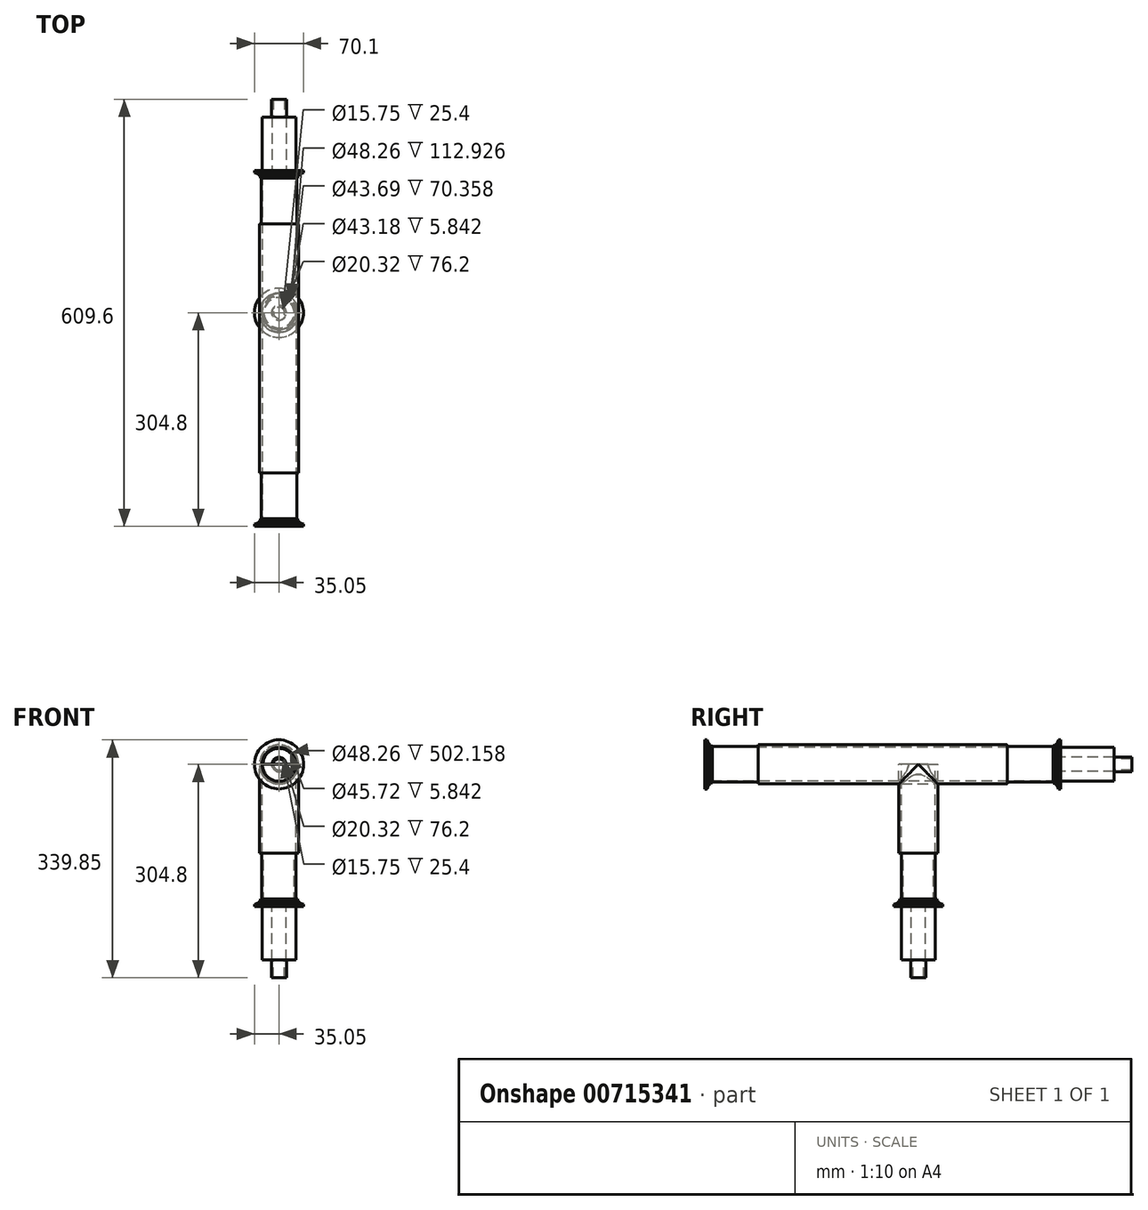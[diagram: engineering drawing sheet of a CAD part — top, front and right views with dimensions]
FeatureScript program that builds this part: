
annotation { "Feature Type Name" : "Feature", "Feature Type Description" : "" }
export const myFeature = defineFeature(function(context is Context, id is Id, definition is map)
    precondition{}
    {
        {
            var Q0;
            Q0=qCreatedBy(makeId("Front.planeOp"),FACE);
            var sketch = newSketch(context, id + "F0", { "sketchPlane" : qUnion([Q0])});
            skCircle(sketch, "E0", {"center": v(0, 0) * mm, "radius": 22.23 * mm, "construction": true});
            skSolve(sketch);
        }
        {
            var Q0;
            Q0=qCreatedBy(makeId("Front.planeOp"),FACE);
            var sketch = newSketch(context, id + "F1", { "sketchPlane" : qUnion([Q0])});
            skCircle(sketch, "E1", {"center": v(0, 0) * mm, "radius": 24.13 * mm});
            skCircle(sketch, "E2", {"center": v(0, 0) * mm, "radius": 35.05 * mm});
            skSolve(sketch);
        }
        {
            var Q0;
            Q0=qSketchRegion(id+"F1",true);
            extrude(context, id + "F2", {"entities" : qUnion([Q0]), "oppositeDirection" : true, "depth" : 5.84 * mm, "offsetDistance" : 25.4 * mm});
        }
        {
            var Q0;
            Q0=makeQuery(id+"F2.opExtrude","CAP_EDGE",EDGE,{"disambiguationData":[OSD([sQuery(id+"F1.wireOp",EDGE,"E2")])],"isStart":false});
            chamfer(context, id + "F3", {"entities" : qUnion([Q0]), "chamferType" : ChamferType.OFFSET_ANGLE, "width" : 2.54 * mm, "oppositeDirection" : false, "angle" : 70 * degree, "tangentPropagation" : true});
        }
        {
            var Q0;
            Q0=makeQuery(id+"F2.opExtrude","CAP_FACE",FACE,{"disambiguationData":[OSD([sQuery(id+"F1.wireOp",EDGE,"E1"),sQuery(id+"F1.wireOp",EDGE,"E2")])],"isStart":false});
            var sketch = newSketch(context, id + "F4", { "sketchPlane" : qUnion([Q0])});
            skCircle(sketch, "E3", {"center": v(0, 0) * mm, "radius": 28.07 * mm});
            skCircle(sketch, "E4", {"center": v(0, 0) * mm, "radius": 24.13 * mm});
            skSolve(sketch);
        }
        {
            var Q0;
            Q0=qSketchRegion(id+"F4",true);
            extrude(context, id + "F5", {"entities" : qUnion([Q0]), "operationType" : NewBodyOperationType.ADD, "depth" : 2.54 * mm, "offsetDistance" : 25.4 * mm});
        }
        {
            var Q0;
            Q0=makeQuery(id+"F5.opExtrude","CAP_FACE",FACE,{"disambiguationData":[OSD([sQuery(id+"F4.wireOp",EDGE,"E3"),sQuery(id+"F4.wireOp",EDGE,"E4")])],"isStart":false});
            var sketch = newSketch(context, id + "F6", { "sketchPlane" : qUnion([Q0])});
            skCircle(sketch, "E5", {"center": v(0, 0) * mm, "radius": 26.55 * mm});
            skCircle(sketch, "E6", {"center": v(0, 0) * mm, "radius": 24.13 * mm});
            skSolve(sketch);
        }
        {
            var Q0;
            Q0=qSketchRegion(id+"F6",true);
            extrude(context, id + "F7", {"entities" : qUnion([Q0]), "operationType" : NewBodyOperationType.ADD, "depth" : 2.54 * mm, "offsetDistance" : 25.4 * mm});
        }
        {
            var Q0;
            Q0=makeQuery(id+"F7.opExtrude","CAP_FACE",FACE,{"disambiguationData":[OSD([sQuery(id+"F6.wireOp",EDGE,"E5"),sQuery(id+"F6.wireOp",EDGE,"E6")])],"isStart":false});
            var sketch = newSketch(context, id + "F8", { "sketchPlane" : qUnion([Q0])});
            skCircle(sketch, "E7", {"center": v(0, 0) * mm, "radius": 24.13 * mm});
            skCircle(sketch, "E8", {"center": v(0, 0) * mm, "radius": 25.4 * mm});
            skSolve(sketch);
        }
        {
            var Q0;
            Q0=qSketchRegion(id+"F8",true);
            extrude(context, id + "F9", {"entities" : qUnion([Q0]), "operationType" : NewBodyOperationType.ADD, "depth" : 65.28 * mm, "offsetDistance" : 25.4 * mm});
        }
        {
            var Q0;
            Q0=makeQuery(id+"F9.opExtrude","CAP_FACE",FACE,{"disambiguationData":[OSD([sQuery(id+"F8.wireOp",EDGE,"E7"),sQuery(id+"F8.wireOp",EDGE,"E8")])],"isStart":false});
            var sketch = newSketch(context, id + "F10", { "sketchPlane" : qUnion([Q0])});
            skCircle(sketch, "E9", {"center": v(0, 0) * mm, "radius": 27.94 * mm});
            skCircle(sketch, "E10", {"center": v(0, 0) * mm, "radius": 24.13 * mm});
            skSolve(sketch);
        }
        {
            var Q0;
            Q0=qCreatedBy(makeId("Right.planeOp"),FACE);
            var sketch = newSketch(context, id + "F11", { "sketchPlane" : qUnion([Q0])});
            skLineSegment(sketch, "E11", {"start": v(76.2, 0) * mm, "end": v(431.8, 0) * mm});
            skSolve(sketch);
        }
        {
            var Q0;
            Q0=qSketchRegion(id+"F10",true);
            var Q1;
            Q1=qConstructionFilter(qBodyType(qCreatedBy(id+"F11",EDGE),BodyType.WIRE),ConstructionObject.NO);
            sweep(context, id + "F12", {"operationType" : NewBodyOperationType.ADD, "profiles" : qUnion([Q0]), "path" : qUnion([Q1])});
        }
        {
            var Q0;
            Q0=makeQuery(id+"F12.opSweep","CAP_FACE",FACE,{"disambiguationData":[OSD([sQuery(id+"F10.wireOp",EDGE,"E9"),sQuery(id+"F10.wireOp",EDGE,"E10"),sQuery(id+"F11.wireOp",VERTEX,"7ykRA0Qg-2DrY-rTCa-7tXY-ZQoEE0Xzwcjr.end")])],"isStart":false});
            var sketch = newSketch(context, id + "F13", { "sketchPlane" : qUnion([Q0])});
            skCircle(sketch, "E12", {"center": v(0, 0) * mm, "radius": 24.13 * mm});
            skCircle(sketch, "E13", {"center": v(0, 0) * mm, "radius": 25.4 * mm});
            skSolve(sketch);
        }
        {
            var Q0;
            Q0=makeQuery(id+"F12.opSweep","CAP_EDGE",EDGE,{"disambiguationData":[OSD([sQuery(id+"F10.wireOp",EDGE,"E9"),sQuery(id+"F11.wireOp",VERTEX,"7ykRA0Qg-2DrY-rTCa-7tXY-ZQoEE0Xzwcjr.end")])],"isStart":false});
            fillet(context, id + "F14", {"entities" : qUnion([Q0]), "radius" : 1.27 * mm, "tangentPropagation" : true, "allowEdgeOverflow" : false});
        }
        {
            var Q0;
            Q0=qSketchRegion(id+"F13",true);
            extrude(context, id + "F15", {"entities" : qUnion([Q0]), "operationType" : NewBodyOperationType.ADD, "depth" : 76.2 * mm, "offsetDistance" : 25.4 * mm});
        }
        {
            var Q0;
            Q0=makeQuery(id+"F15.opExtrude","CAP_FACE",FACE,{"disambiguationData":[OSD([sQuery(id+"F13.wireOp",EDGE,"E12"),sQuery(id+"F13.wireOp",EDGE,"E13")])],"isStart":false});
            var sketch = newSketch(context, id + "F16", { "sketchPlane" : qUnion([Q0])});
            skCircle(sketch, "E14", {"center": v(0, 0) * mm, "radius": 35.05 * mm});
            skCircle(sketch, "E15", {"center": v(0, 0) * mm, "radius": 22.86 * mm});
            skSolve(sketch);
        }
        {
            var Q0;
            Q0=qSketchRegion(id+"F16",true);
            extrude(context, id + "F17", {"entities" : qUnion([Q0]), "operationType" : NewBodyOperationType.ADD, "oppositeDirection" : true, "depth" : 5.84 * mm, "offsetDistance" : 25.4 * mm});
        }
        {
            var Q0;
            Q0=makeQuery(id+"F17.opExtrude","CAP_EDGE",EDGE,{"disambiguationData":[OSD([sQuery(id+"F16.wireOp",EDGE,"E14")])],"isStart":false});
            chamfer(context, id + "F18", {"entities" : qUnion([Q0]), "chamferType" : ChamferType.OFFSET_ANGLE, "width" : 2.54 * mm, "oppositeDirection" : false, "angle" : 70 * degree, "tangentPropagation" : true});
        }
        {
            var Q0;
            Q0=makeQuery(id+"F17.opExtrude","CAP_FACE",FACE,{"disambiguationData":[OSD([sQuery(id+"F16.wireOp",EDGE,"E14"),sQuery(id+"F16.wireOp",EDGE,"E15")])],"isStart":false});
            var sketch = newSketch(context, id + "F19", { "sketchPlane" : qUnion([Q0])});
            skCircle(sketch, "E16", {"center": v(0, 0) * mm, "radius": 24.13 * mm});
            skCircle(sketch, "E17", {"center": v(0, 0) * mm, "radius": 28.07 * mm});
            skSolve(sketch);
        }
        {
            var Q0;
            Q0=qSketchRegion(id+"F19",true);
            extrude(context, id + "F20", {"entities" : qUnion([Q0]), "operationType" : NewBodyOperationType.ADD, "depth" : 2.54 * mm, "offsetDistance" : 25.4 * mm});
        }
        {
            var Q0;
            Q0=makeQuery(id+"F20.opExtrude","CAP_FACE",FACE,{"disambiguationData":[OSD([sQuery(id+"F19.wireOp",EDGE,"E16"),sQuery(id+"F19.wireOp",EDGE,"E17")])],"isStart":false});
            var sketch = newSketch(context, id + "F21", { "sketchPlane" : qUnion([Q0])});
            skCircle(sketch, "E18", {"center": v(0, 0) * mm, "radius": 24.13 * mm});
            skCircle(sketch, "E19", {"center": v(0, 0) * mm, "radius": 26.8 * mm});
            skSolve(sketch);
        }
        {
            var Q0;
            Q0=qSketchRegion(id+"F21",true);
            extrude(context, id + "F22", {"entities" : qUnion([Q0]), "operationType" : NewBodyOperationType.ADD, "depth" : 2.54 * mm, "offsetDistance" : 25.4 * mm});
        }
        {
            var Q0;
            Q0=makeQuery(id+"F17.boolean.opBoolean","MERGE",FACE,{"derivedFrom":[makeQuery(id+"F15.opExtrude","CAP_FACE",FACE,{"disambiguationData":[OSD([sQuery(id+"F13.wireOp",EDGE,"E12"),sQuery(id+"F13.wireOp",EDGE,"E13")])],"isStart":false}),makeQuery(id+"F17.opExtrude","CAP_FACE",FACE,{"disambiguationData":[OSD([sQuery(id+"F16.wireOp",EDGE,"E14"),sQuery(id+"F16.wireOp",EDGE,"E15")])],"isStart":true})]});
            var sketch = newSketch(context, id + "F23", { "sketchPlane" : qUnion([Q0])});
            skCircle(sketch, "E20", {"center": v(0, 0) * mm, "radius": 10.16 * mm});
            skCircle(sketch, "E21", {"center": v(0, 0) * mm, "radius": 24.13 * mm});
            skSolve(sketch);
        }
        {
            var Q0;
            Q0=qSketchRegion(id+"F23",true);
            extrude(context, id + "F24", {"entities" : qUnion([Q0]), "operationType" : NewBodyOperationType.ADD, "depth" : 76.2 * mm, "offsetDistance" : 25.4 * mm});
        }
        {
            var Q0;
            Q0=makeQuery(id+"F24.opExtrude","CAP_FACE",FACE,{"disambiguationData":[OSD([sQuery(id+"F23.wireOp",EDGE,"E20"),sQuery(id+"F23.wireOp",EDGE,"E21")])],"isStart":false});
            var sketch = newSketch(context, id + "F25", { "sketchPlane" : qUnion([Q0])});
            skCircle(sketch, "E22", {"center": v(0, 0) * mm, "radius": 10.67 * mm});
            skCircle(sketch, "E23", {"center": v(0, 0) * mm, "radius": 7.87 * mm});
            skSolve(sketch);
        }
        {
            var Q0;
            Q0=qSketchRegion(id+"F25",true);
            extrude(context, id + "F26", {"entities" : qUnion([Q0]), "operationType" : NewBodyOperationType.ADD, "depth" : 25.4 * mm, "offsetDistance" : 25.4 * mm});
        }
        {
            var Q0;
            Q0=qCreatedBy(makeId("Right.planeOp"),FACE);
            var sketch = newSketch(context, id + "F27", { "sketchPlane" : qUnion([Q0])});
            skLineSegment(sketch, "E24", {"start": v(0, 0) * mm, "end": v(609.6, 0) * mm});
            skSolve(sketch);
        }
        {
            var Q0;
            Q0=qCreatedBy(makeId("Top.planeOp"),FACE);
            var sketch = newSketch(context, id + "F28", { "sketchPlane" : qUnion([Q0])});
            skCircle(sketch, "E25", {"center": v(0, 304.8) * mm, "radius": 27.94 * mm});
            skCircle(sketch, "E26", {"center": v(0, 304.8) * mm, "radius": 24.13 * mm});
            skSolve(sketch);
        }
        {
            var Q0;
            Q0 = qSketchRegion(id + "F28", true);
            extrude(context, id + "F29", {"entities" : qUnion([Q0]), "operationType" : NewBodyOperationType.ADD, "oppositeDirection" : true, "depth" : 127 * mm, "offsetDistance" : 25.4 * mm});
        }
        {
            var Q0;
            Q0=makeQuery(id+"F29.opExtrude","CAP_FACE",FACE,{"disambiguationData":[OSD([sQuery(id+"F28.wireOp",EDGE,"E25"),sQuery(id+"F28.wireOp",EDGE,"E26")])],"isStart":false});
            var sketch = newSketch(context, id + "F30", { "sketchPlane" : qUnion([Q0])});
            skCircle(sketch, "E27", {"center": v(0, -304.8) * mm, "radius": 24.38 * mm});
            skCircle(sketch, "E28", {"center": v(0, -304.8) * mm, "radius": 21.84 * mm});
            skSolve(sketch);
        }
        {
            var Q0;
            Q0 = qSketchRegion(id + "F30", true);
            extrude(context, id + "F31", {"entities" : qUnion([Q0]), "operationType" : NewBodyOperationType.ADD, "depth" : 76.2 * mm, "offsetDistance" : 25.4 * mm});
        }
        {
            var Q0;
            Q0=makeQuery(id+"F31.opExtrude","CAP_FACE",FACE,{"disambiguationData":[OSD([sQuery(id+"F30.wireOp",EDGE,"E27"),sQuery(id+"F30.wireOp",EDGE,"E28")])],"isStart":false});
            var sketch = newSketch(context, id + "F32", { "sketchPlane" : qUnion([Q0])});
            skCircle(sketch, "E29", {"center": v(0, -304.8) * mm, "radius": 21.59 * mm});
            skCircle(sketch, "E30", {"center": v(0, -304.8) * mm, "radius": 35.05 * mm});
            skSolve(sketch);
        }
        {
            var Q0;
            Q0 = qSketchRegion(id + "F32", true);
            extrude(context, id + "F33", {"entities" : qUnion([Q0]), "operationType" : NewBodyOperationType.ADD, "oppositeDirection" : true, "depth" : 5.84 * mm, "offsetDistance" : 25.4 * mm});
        }
        {
            var Q0;
            Q0=makeQuery(id+"F33.opExtrude","CAP_EDGE",EDGE,{"disambiguationData":[OSD([sQuery(id+"F32.wireOp",EDGE,"E30")])],"isStart":false});
            chamfer(context, id + "F34", {"entities" : qUnion([Q0]), "chamferType" : ChamferType.OFFSET_ANGLE, "width" : 2.54 * mm, "oppositeDirection" : false, "angle" : 70 * degree, "tangentPropagation" : true});
        }
        {
            var Q0;
            Q0=makeQuery(id+"F33.opExtrude","CAP_FACE",FACE,{"disambiguationData":[OSD([sQuery(id+"F32.wireOp",EDGE,"E29"),sQuery(id+"F32.wireOp",EDGE,"E30")])],"isStart":false});
            var sketch = newSketch(context, id + "F35", { "sketchPlane" : qUnion([Q0])});
            skCircle(sketch, "E31", {"center": v(0, 304.8) * mm, "radius": 28.07 * mm});
            skCircle(sketch, "E32", {"center": v(0, 304.8) * mm, "radius": 24.38 * mm});
            skSolve(sketch);
        }
        {
            var Q0;
            Q0 = qSketchRegion(id + "F35", true);
            extrude(context, id + "F36", {"entities" : qUnion([Q0]), "operationType" : NewBodyOperationType.ADD, "depth" : 2.54 * mm, "offsetDistance" : 25.4 * mm});
        }
        {
            var Q0;
            Q0=makeQuery(id+"F36.opExtrude","CAP_FACE",FACE,{"disambiguationData":[OSD([sQuery(id+"F35.wireOp",EDGE,"E31"),sQuery(id+"F35.wireOp",EDGE,"E32")])],"isStart":false});
            var sketch = newSketch(context, id + "F37", { "sketchPlane" : qUnion([Q0])});
            skCircle(sketch, "E33", {"center": v(0, 304.8) * mm, "radius": 26.8 * mm});
            skCircle(sketch, "E34", {"center": v(0, 304.8) * mm, "radius": 24.38 * mm});
            skSolve(sketch);
        }
        {
            var Q0;
            Q0 = qSketchRegion(id + "F37", true);
            extrude(context, id + "F38", {"entities" : qUnion([Q0]), "operationType" : NewBodyOperationType.ADD, "depth" : 2.54 * mm, "offsetDistance" : 25.4 * mm});
        }
        {
            var Q0;
            Q0=makeQuery(id+"F33.boolean.opBoolean","MERGE",FACE,{"derivedFrom":[makeQuery(id+"F31.opExtrude","CAP_FACE",FACE,{"disambiguationData":[OSD([sQuery(id+"F30.wireOp",EDGE,"E27"),sQuery(id+"F30.wireOp",EDGE,"E28")])],"isStart":false}),makeQuery(id+"F33.opExtrude","CAP_FACE",FACE,{"disambiguationData":[OSD([sQuery(id+"F32.wireOp",EDGE,"E29"),sQuery(id+"F32.wireOp",EDGE,"E30")])],"isStart":true})]});
            var sketch = newSketch(context, id + "F39", { "sketchPlane" : qUnion([Q0])});
            skCircle(sketch, "E35", {"center": v(0, -304.8) * mm, "radius": 10.16 * mm});
            skCircle(sketch, "E36", {"center": v(0, -304.8) * mm, "radius": 24.13 * mm});
            skSolve(sketch);
        }
        {
            var Q0;
            Q0 = qSketchRegion(id + "F39", true);
            extrude(context, id + "F40", {"entities" : qUnion([Q0]), "operationType" : NewBodyOperationType.ADD, "depth" : 76.2 * mm, "offsetDistance" : 25.4 * mm});
        }
        {
            var Q0;
            Q0=makeQuery(id+"F40.opExtrude","CAP_FACE",FACE,{"disambiguationData":[OSD([sQuery(id+"F39.wireOp",EDGE,"E35"),sQuery(id+"F39.wireOp",EDGE,"E36")])],"isStart":false});
            var sketch = newSketch(context, id + "F41", { "sketchPlane" : qUnion([Q0])});
            skCircle(sketch, "E37", {"center": v(0, -304.8) * mm, "radius": 10.67 * mm});
            skCircle(sketch, "E38", {"center": v(0, -304.8) * mm, "radius": 7.87 * mm});
            skSolve(sketch);
        }
        {
            var Q0;
            Q0 = qSketchRegion(id + "F41", true);
            extrude(context, id + "F42", {"entities" : qUnion([Q0]), "operationType" : NewBodyOperationType.ADD, "depth" : 25.4 * mm, "offsetDistance" : 25.4 * mm});
        }
    });
